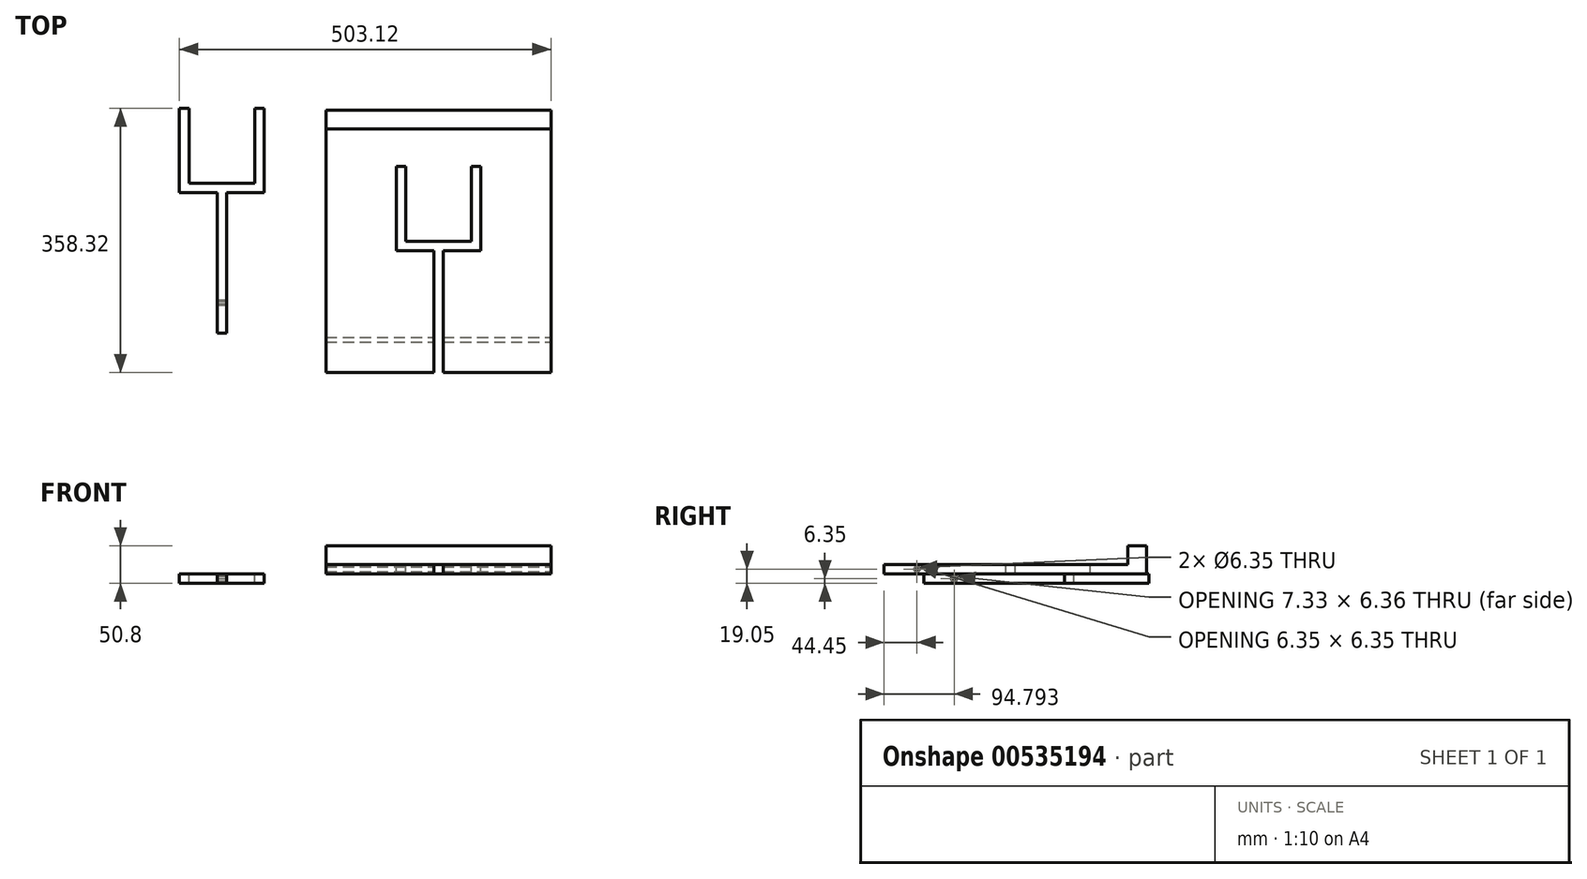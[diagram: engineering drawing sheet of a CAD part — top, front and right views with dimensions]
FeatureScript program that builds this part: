
annotation { "Feature Type Name" : "Feature", "Feature Type Description" : "" }
export const myFeature = defineFeature(function(context is Context, id is Id, definition is map)
    precondition{}
    {
        {
            var Q0;
            Q0=qCreatedBy(makeId("Top.planeOp"),FACE);
            var sketch = newSketch(context, id + "F0", { "sketchPlane" : qUnion([Q0])});
            skLineSegment(sketch, "E0.bottom", {"start": v(-152.4, -177.8) * mm, "end": v(152.4, -177.8) * mm});
            skLineSegment(sketch, "E0.top", {"start": v(-152.4, 177.8) * mm, "end": v(152.4, 177.8) * mm});
            skLineSegment(sketch, "E0.left", {"start": v(-152.4, -177.8) * mm, "end": v(-152.4, 177.8) * mm});
            skLineSegment(sketch, "E0.right", {"start": v(152.4, -177.8) * mm, "end": v(152.4, 177.8) * mm});
            skPoint(sketch, "E0.middle", {"position": v(0, 0) * mm});
            skLineSegment(sketch, "E1.top", {"start": v(-152.4, 152.4) * mm, "end": v(152.4, 152.4) * mm});
            skLineSegment(sketch, "E1.left", {"start": v(-152.4, 177.8) * mm, "end": v(-152.4, 152.4) * mm});
            skLineSegment(sketch, "E1.right", {"start": v(152.4, 177.8) * mm, "end": v(152.4, 152.4) * mm});
            skSolve(sketch);
        }
        {
            var Q0;
            Q0=makeQuery(id+"F0.imprint","IMPRINT",FACE,{"disambiguationData":[TD([[makeQuery(id+"F0.imprint","IMPRINT",EDGE,{"derivedFrom":sQuery(id+"F0.wireOp",EDGE,"E0.bottom")}),1.0]])]});
            extrude(context, id + "F1", {"entities" : qUnion([Q0]), "depth" : 12.7 * mm});
        }
        {
            var Q0;
            Q0=makeQuery(id+"F1.opExtrude","CAP_FACE",FACE,{"disambiguationData":[OSD([sQuery(id+"F0.wireOp",EDGE,"E0.bottom"),sQuery(id+"F0.wireOp",EDGE,"E0.top"),sQuery(id+"F0.wireOp",EDGE,"E0.left"),sQuery(id+"F0.wireOp",EDGE,"E0.right")])],"isStart":false});
            var sketch = newSketch(context, id + "F2", { "sketchPlane" : qUnion([Q0])});
            skLineSegment(sketch, "E2.bottom", {"start": v(6.35, -177.8) * mm, "end": v(-6.35, -177.8) * mm});
            skLineSegment(sketch, "E2.top", {"start": v(6.35, 0) * mm, "end": v(-6.35, 0) * mm});
            skLineSegment(sketch, "E2.left", {"start": v(6.35, -177.8) * mm, "end": v(6.35, 0) * mm});
            skLineSegment(sketch, "E2.right", {"start": v(-6.35, -177.8) * mm, "end": v(-6.35, 0) * mm});
            skPoint(sketch, "E2.middle", {"position": v(0, -88.9) * mm});
            skLineSegment(sketch, "E3.bottom", {"start": v(-6.35, 0) * mm, "end": v(-57.15, 0) * mm});
            skLineSegment(sketch, "E3.top", {"start": v(-6.35, -12.7) * mm, "end": v(-57.15, -12.7) * mm});
            skLineSegment(sketch, "E3.left", {"start": v(-6.35, 0) * mm, "end": v(-6.35, -12.7) * mm});
            skLineSegment(sketch, "E3.right", {"start": v(-57.15, 0) * mm, "end": v(-57.15, -12.7) * mm});
            skLineSegment(sketch, "E4.bottom", {"start": v(6.35, 0) * mm, "end": v(57.15, 0) * mm});
            skLineSegment(sketch, "E4.top", {"start": v(6.35, -12.7) * mm, "end": v(57.15, -12.7) * mm});
            skLineSegment(sketch, "E4.left", {"start": v(6.35, 0) * mm, "end": v(6.35, -12.7) * mm});
            skLineSegment(sketch, "E4.right", {"start": v(57.15, 0) * mm, "end": v(57.15, -12.7) * mm});
            skLineSegment(sketch, "E5.bottom", {"start": v(-57.15, 0) * mm, "end": v(-44.45, 0) * mm});
            skLineSegment(sketch, "E5.top", {"start": v(-57.15, 101.6) * mm, "end": v(-44.45, 101.6) * mm});
            skLineSegment(sketch, "E5.left", {"start": v(-57.15, 0) * mm, "end": v(-57.15, 101.6) * mm});
            skLineSegment(sketch, "E5.right", {"start": v(-44.45, 0) * mm, "end": v(-44.45, 101.6) * mm});
            skLineSegment(sketch, "E6.bottom", {"start": v(57.15, 0) * mm, "end": v(44.45, 0) * mm});
            skLineSegment(sketch, "E6.top", {"start": v(57.15, 101.6) * mm, "end": v(44.45, 101.6) * mm});
            skLineSegment(sketch, "E6.left", {"start": v(57.15, 0) * mm, "end": v(57.15, 101.6) * mm});
            skLineSegment(sketch, "E6.right", {"start": v(44.45, 0) * mm, "end": v(44.45, 101.6) * mm});
            skSolve(sketch);
        }
        {
            var Q0;
            Q0=qSketchRegion(id+"F2",true);
            extrude(context, id + "F3", {"entities" : qUnion([Q0]), "operationType" : NewBodyOperationType.REMOVE, "oppositeDirection" : true, "depth" : 25.4 * mm});
        }
        {
            var Q0;
            Q0=makeQuery(id+"F3.boolean.opBoolean","COPY",FACE,{"derivedFrom":makeQuery(id+"F3.opExtrude","SWEPT_FACE",FACE,{"disambiguationData":[OSD([sQuery(id+"F2.wireOp",EDGE,"E2.right")])]})});
            var sketch = newSketch(context, id + "F4", { "sketchPlane" : qUnion([Q0])});
            skLineSegment(sketch, "E7", {"start": v(-177.8, 12.7) * mm, "end": v(-133.35, 12.7) * mm});
            skLineSegment(sketch, "E8", {"start": v(-133.35, 12.7) * mm, "end": v(-133.35, 0) * mm});
            skPoint(sketch, "E9", {"position": v(-133.35, 6.35) * mm});
            skCircle(sketch, "E10", {"center": v(-133.35, 6.35) * mm, "radius": 3.18 * mm});
            skSolve(sketch);
        }
        {
            var Q0;
            Q0=qSketchRegion(id+"F4",true);
            extrude(context, id + "F5", {"entities" : qUnion([Q0]), "operationType" : NewBodyOperationType.REMOVE, "oppositeDirection" : true, "depth" : 203.2 * mm, "hasSecondDirection" : true, "secondDirectionOppositeDirection" : false, "secondDirectionDepth" : 203.2 * mm});
        }
        {
            var Q0;
            Q0=qCreatedBy(makeId("Top.planeOp"),FACE);
            var sketch = newSketch(context, id + "F6", { "sketchPlane" : qUnion([Q0])});
            skLineSegment(sketch, "E11", {"start": v(-299.92, -124.28) * mm, "end": v(-299.92, 66.22) * mm});
            skLineSegment(sketch, "E12", {"start": v(-299.92, 66.22) * mm, "end": v(-350.72, 66.22) * mm});
            skLineSegment(sketch, "E13", {"start": v(-350.72, 66.22) * mm, "end": v(-350.72, 180.52) * mm});
            skLineSegment(sketch, "E14", {"start": v(-350.72, 180.52) * mm, "end": v(-338.02, 180.52) * mm});
            skLineSegment(sketch, "E15", {"start": v(-338.02, 180.52) * mm, "end": v(-338.02, 78.92) * mm});
            skLineSegment(sketch, "E16", {"start": v(-338.02, 78.92) * mm, "end": v(-249.12, 78.92) * mm});
            skLineSegment(sketch, "E17", {"start": v(-249.12, 78.92) * mm, "end": v(-249.12, 180.52) * mm});
            skLineSegment(sketch, "E18", {"start": v(-249.12, 180.52) * mm, "end": v(-236.42, 180.52) * mm});
            skLineSegment(sketch, "E19", {"start": v(-236.42, 180.52) * mm, "end": v(-236.42, 66.22) * mm});
            skLineSegment(sketch, "E20", {"start": v(-236.42, 66.22) * mm, "end": v(-287.22, 66.22) * mm});
            skLineSegment(sketch, "E21", {"start": v(-287.22, 66.22) * mm, "end": v(-287.22, -124.28) * mm});
            skLineSegment(sketch, "E22", {"start": v(-287.22, -124.28) * mm, "end": v(-299.92, -124.28) * mm});
            skPoint(sketch, "E23", {"position": v(-287.22, -83) * mm});
            skSolve(sketch);
        }
        {
            var Q0;
            Q0=makeQuery(id+"F6.imprint","IMPRINT",FACE,{"disambiguationData":[TD([[makeQuery(id+"F6.imprint","IMPRINT",EDGE,{"derivedFrom":sQuery(id+"F6.wireOp",EDGE,"E11")}),-1.0]])]});
            extrude(context, id + "F7", {"entities" : qUnion([Q0]), "oppositeDirection" : true, "depth" : 12.7 * mm});
        }
        {
            var Q0;
            Q0=makeQuery(id+"F7.opExtrude","SWEPT_FACE",FACE,{"disambiguationData":[OSD([sQuery(id+"F6.wireOp",EDGE,"E21")])]});
            var sketch = newSketch(context, id + "F8", { "sketchPlane" : qUnion([Q0])});
            skCircle(sketch, "E24.cCircle", {"center": v(-83, -6.35) * mm, "radius": 3.18 * mm, "construction": true});
            skLineSegment(sketch, "E24.0", {"start": v(-84.83, -9.53) * mm, "end": v(-86.67, -6.36) * mm});
            skLineSegment(sketch, "E24.1", {"start": v(-86.67, -6.36) * mm, "end": v(-84.85, -3.18) * mm});
            skLineSegment(sketch, "E24.2", {"start": v(-84.85, -3.18) * mm, "end": v(-81.19, -3.17) * mm});
            skLineSegment(sketch, "E24.3", {"start": v(-81.19, -3.17) * mm, "end": v(-79.34, -6.34) * mm});
            skLineSegment(sketch, "E24.4", {"start": v(-79.34, -6.34) * mm, "end": v(-81.16, -9.52) * mm});
            skLineSegment(sketch, "E24.5", {"start": v(-81.16, -9.52) * mm, "end": v(-84.83, -9.53) * mm});
            skPoint(sketch, "E24.0.midPoint", {"position": v(-85.75, -7.95) * mm});
            skSolve(sketch);
        }
        {
            var Q0;
            Q0=makeQuery(id+"F8.imprint","IMPRINT",FACE,{"disambiguationData":[TD([[makeQuery(id+"F8.imprint","IMPRINT",EDGE,{"derivedFrom":sQuery(id+"F8.wireOp",EDGE,"E24.0")}),-1.0]])]});
            extrude(context, id + "F9", {"entities" : qUnion([Q0]), "operationType" : NewBodyOperationType.REMOVE, "oppositeDirection" : true, "depth" : 12.7 * mm});
        }
        {
            var Q0;
            Q0=makeQuery(id+"F0.imprint","IMPRINT",FACE,{"disambiguationData":[TD([[makeQuery(id+"F0.imprint","IMPRINT",EDGE,{"derivedFrom":sQuery(id+"F0.wireOp",EDGE,"E0.top")}),-1.0]])]});
            extrude(context, id + "F10", {"entities" : qUnion([Q0]), "operationType" : NewBodyOperationType.ADD, "depth" : 38.1 * mm});
        }
    });
